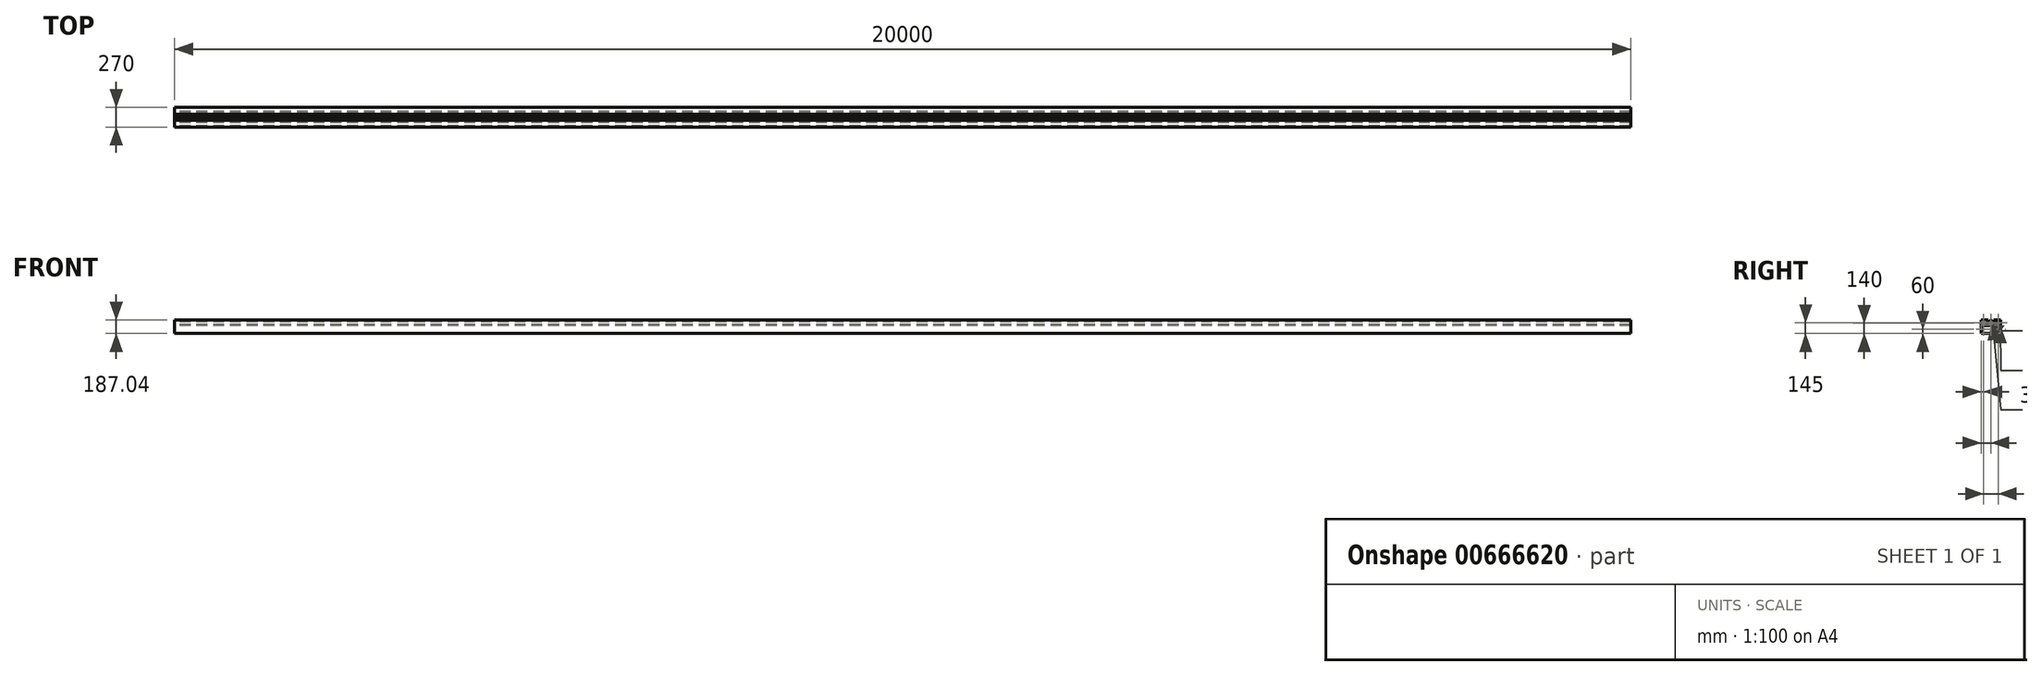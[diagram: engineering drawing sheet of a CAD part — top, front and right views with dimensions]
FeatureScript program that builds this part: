
annotation { "Feature Type Name" : "Feature", "Feature Type Description" : "" }
export const myFeature = defineFeature(function(context is Context, id is Id, definition is map)
    precondition{}
    {
        {
            var Q0;
            Q0=qCreatedBy(makeId("Right.planeOp"),FACE);
            var sketch = newSketch(context, id + "F0", { "sketchPlane" : qUnion([Q0])});
            skLineSegment(sketch, "E0", {"start": v(157.48, 0) * mm, "end": v(157.48, -180) * mm});
            skLineSegment(sketch, "E1", {"start": v(157.48, -180) * mm, "end": v(-102.52, -180) * mm});
            skLineSegment(sketch, "E2", {"start": v(-102.52, -180) * mm, "end": v(-102.52, 0) * mm});
            skLineSegment(sketch, "E3", {"start": v(-102.52, 0) * mm, "end": v(-102.52, -10) * mm});
            skLineSegment(sketch, "E4", {"start": v(157.48, 0) * mm, "end": v(157.48, -10) * mm});
            skLineSegment(sketch, "E5.bottom", {"start": v(-102.52, -10) * mm, "end": v(-42.52, -10) * mm});
            skLineSegment(sketch, "E5.top", {"start": v(-102.52, -70) * mm, "end": v(-42.52, -70) * mm});
            skLineSegment(sketch, "E5.left", {"start": v(-102.52, -10) * mm, "end": v(-102.52, -70) * mm});
            skLineSegment(sketch, "E5.right", {"start": v(-42.52, -10) * mm, "end": v(-42.52, -70) * mm});
            skLineSegment(sketch, "E6.bottom", {"start": v(157.48, -10) * mm, "end": v(97.48, -10) * mm});
            skLineSegment(sketch, "E6.top", {"start": v(157.48, -70) * mm, "end": v(97.48, -70) * mm});
            skLineSegment(sketch, "E6.left", {"start": v(157.48, -10) * mm, "end": v(157.48, -70) * mm});
            skLineSegment(sketch, "E6.right", {"start": v(97.48, -10) * mm, "end": v(97.48, -70) * mm});
            skLineSegment(sketch, "E7", {"start": v(-102.52, -10) * mm, "end": v(-102.52, -15) * mm});
            skLineSegment(sketch, "E8", {"start": v(157.48, -10) * mm, "end": v(157.48, -15) * mm});
            skLineSegment(sketch, "E9", {"start": v(-102.52, 0) * mm, "end": v(-107.52, 0) * mm});
            skLineSegment(sketch, "E10", {"start": v(-107.52, 0) * mm, "end": v(-107.52, -185) * mm});
            skLineSegment(sketch, "E11", {"start": v(-107.52, -185) * mm, "end": v(162.48, -185) * mm});
            skLineSegment(sketch, "E12", {"start": v(162.48, -185) * mm, "end": v(162.48, 0) * mm});
            skLineSegment(sketch, "E13", {"start": v(162.48, 0) * mm, "end": v(157.48, 0) * mm});
            skLineSegment(sketch, "E14", {"start": v(-92.52, -70) * mm, "end": v(147.48, -70) * mm});
            skLineSegment(sketch, "E15", {"start": v(-92.52, -70) * mm, "end": v(-92.52, -75) * mm});
            skLineSegment(sketch, "E16", {"start": v(-92.52, -75) * mm, "end": v(147.48, -75) * mm});
            skLineSegment(sketch, "E17", {"start": v(147.48, -75) * mm, "end": v(147.48, -70) * mm});
            skLineSegment(sketch, "E18.bottom", {"start": v(152.48, -15) * mm, "end": v(102.48, -15) * mm});
            skLineSegment(sketch, "E18.top", {"start": v(152.48, -65) * mm, "end": v(102.48, -65) * mm});
            skLineSegment(sketch, "E18.left", {"start": v(152.48, -15) * mm, "end": v(152.48, -65) * mm});
            skLineSegment(sketch, "E18.right", {"start": v(102.48, -15) * mm, "end": v(102.48, -65) * mm});
            skLineSegment(sketch, "E19.bottom", {"start": v(-97.52, -15) * mm, "end": v(-47.52, -15) * mm});
            skLineSegment(sketch, "E19.top", {"start": v(-97.52, -65) * mm, "end": v(-47.52, -65) * mm});
            skLineSegment(sketch, "E19.left", {"start": v(-97.52, -15) * mm, "end": v(-97.52, -65) * mm});
            skLineSegment(sketch, "E19.right", {"start": v(-47.52, -15) * mm, "end": v(-47.52, -65) * mm});
            skLineSegment(sketch, "E20.bottom", {"start": v(2.48, -69.96) * mm, "end": v(52.48, -69.96) * mm});
            skLineSegment(sketch, "E20.top", {"start": v(2.48, -19.96) * mm, "end": v(52.48, -19.96) * mm});
            skLineSegment(sketch, "E20.left", {"start": v(2.48, -69.96) * mm, "end": v(2.48, -19.96) * mm});
            skLineSegment(sketch, "E20.right", {"start": v(52.48, -69.96) * mm, "end": v(52.48, -19.96) * mm});
            skLineSegment(sketch, "E21", {"start": v(2.48, -69.96) * mm, "end": v(7.48, -70) * mm});
            skLineSegment(sketch, "E22.bottom", {"start": v(7.48, -65) * mm, "end": v(47.48, -65) * mm});
            skLineSegment(sketch, "E22.top", {"start": v(7.48, -25) * mm, "end": v(47.48, -25) * mm});
            skLineSegment(sketch, "E22.left", {"start": v(7.48, -65) * mm, "end": v(7.48, -25) * mm});
            skLineSegment(sketch, "E22.right", {"start": v(47.48, -65) * mm, "end": v(47.48, -25) * mm});
            skLineSegment(sketch, "E23", {"start": v(27.48, 2.04) * mm, "end": v(7.05, -19.96) * mm});
            skLineSegment(sketch, "E24", {"start": v(7.05, -19.96) * mm, "end": v(10.05, -19.96) * mm});
            skLineSegment(sketch, "E25", {"start": v(10.05, -19.96) * mm, "end": v(27.48, -1.2) * mm});
            skLineSegment(sketch, "E26", {"start": v(27.48, 2.04) * mm, "end": v(47.9, -19.96) * mm});
            skLineSegment(sketch, "E27", {"start": v(47.9, -19.96) * mm, "end": v(44.9, -19.96) * mm});
            skLineSegment(sketch, "E28", {"start": v(44.9, -19.96) * mm, "end": v(27.48, -1.2) * mm});
            skLineSegment(sketch, "E29.bottom", {"start": v(-102.52, -10) * mm, "end": v(-12.52, -10) * mm});
            skLineSegment(sketch, "E29.top", {"start": v(-102.52, 0) * mm, "end": v(-12.52, 0) * mm});
            skLineSegment(sketch, "E29.left", {"start": v(-102.52, -10) * mm, "end": v(-102.52, 0) * mm});
            skLineSegment(sketch, "E29.right", {"start": v(-12.52, -10) * mm, "end": v(-12.52, 0) * mm});
            skLineSegment(sketch, "E30.bottom", {"start": v(157.48, -10) * mm, "end": v(67.48, -10) * mm});
            skLineSegment(sketch, "E30.top", {"start": v(157.48, 0) * mm, "end": v(67.48, 0) * mm});
            skLineSegment(sketch, "E30.left", {"start": v(157.48, -10) * mm, "end": v(157.48, 0) * mm});
            skLineSegment(sketch, "E30.right", {"start": v(67.48, -10) * mm, "end": v(67.48, 0) * mm});
            skSolve(sketch);
        }
        {
            var Q0;
            Q0=makeQuery(id+"F0.imprint","IMPRINT",FACE,{"disambiguationData":[TD([[makeQuery(id+"F0.imprint","IMPRINT",EDGE,{"derivedFrom":sQuery(id+"F0.wireOp",EDGE,"E29.top")}),-1.0]])]});
            var Q1;
            {var subQ2=sQuery(id+"F0.wireOp",EDGE,"E5.top");Q1=makeQuery(id+"F0.imprint","IMPRINT",FACE,{"disambiguationData":[TD([[makeQuery(id+"F0.imprint","IMPRINT",EDGE,{"derivedFrom":subQ2}),1.0]])]});}
            var Q2;
            Q2=makeQuery(id+"F0.imprint","IMPRINT",FACE,{"disambiguationData":[TD([[makeQuery(id+"F0.imprint","IMPRINT",EDGE,{"derivedFrom":sQuery(id+"F0.wireOp",EDGE,"E0")}),1.0]])]});
            var Q3;
            {var subQ5=sQuery(id+"F0.wireOp",EDGE,"E15");Q3=makeQuery(id+"F0.imprint","IMPRINT",FACE,{"disambiguationData":[TD([[makeQuery(id+"F0.imprint","IMPRINT",EDGE,{"derivedFrom":subQ5}),1.0]])]});}
            var Q4;
            Q4=makeQuery(id+"F0.imprint","IMPRINT",FACE,{"disambiguationData":[TD([[makeQuery(id+"F0.imprint","IMPRINT",EDGE,{"derivedFrom":sQuery(id+"F0.wireOp",EDGE,"E20.bottom")}),1.0]])]});
            var Q5;
            Q5=makeQuery(id+"F0.imprint","IMPRINT",FACE,{"disambiguationData":[TD([[makeQuery(id+"F0.imprint","IMPRINT",EDGE,{"derivedFrom":sQuery(id+"F0.wireOp",EDGE,"E23")}),1.0]])]});
            var Q6;
            Q6=makeQuery(id+"F0.imprint","IMPRINT",FACE,{"disambiguationData":[TD([[makeQuery(id+"F0.imprint","IMPRINT",EDGE,{"derivedFrom":sQuery(id+"F0.wireOp",EDGE,"E30.top")}),1.0]])]});
            var Q7;
            {var subQ3=sQuery(id+"F0.wireOp",EDGE,"E6.top");Q7=makeQuery(id+"F0.imprint","IMPRINT",FACE,{"disambiguationData":[TD([[makeQuery(id+"F0.imprint","IMPRINT",EDGE,{"derivedFrom":subQ3}),-1.0]])]});}
            extrude(context, id + "F1", {"entities" : qUnion([Q0, Q1, Q2, Q3, Q4, Q5, Q6, Q7]), "depth" : 20000 * mm, "offsetDistance" : 25 * mm});
        }
    });
